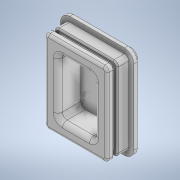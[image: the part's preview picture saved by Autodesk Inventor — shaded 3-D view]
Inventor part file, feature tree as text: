
AUTODESK INVENTOR PART (.ipt)
format: ipt  version: 2021 (Build 250183000, 183)  size: 454,144 bytes
history: native  units: mm
features: extrude x11, sketch x10, projected_geometry x5, chamfer x3, fillet x3
ambient origin geometry x8: Origin, YZ Plane, XZ Plane, XY Plane, X Axis, Y Axis, Z Axis, Center Point
bodies: Body1 (feature_tree)
feature tree (32):
  sketch  "Boceto1"  dims[d17=27.75mm d18=36.38mm]
  extrude  "Extrusión5"  Depth=36.38mm
  extrude  "Extrusión6"  Depth=2.0mm
  chamfer  "Chaflán2"  Distance=3.0mm
  extrude  "Extrusión7"  Depth=1.5mm TaperAngle=45.0deg
  extrude  "Extrusión8"  Depth=5.0mm
  extrude  "Extrusión9"  Depth=5.0mm
  chamfer  "Chaflán3"  Distance=5.0mm
  chamfer  "Chaflán4"  Distance=1.2mm
  extrude  "Extrusión11"  Depth=0.8mm TaperAngle=45.0deg
  fillet  "Empalme4"  Radius=10.0mm
  extrude  "Extrusión12"  Depth=2.0mm
  extrude  "Extrusión13"  Depth=10.0mm TaperAngle=0.0deg
  extrude  "Extrusión14"  Depth=2.0mm
  extrude  "Extrusión15"  Depth=2.0mm TaperAngle=0.0deg
  extrude  "Extrusión16"  Depth=2.0mm
  fillet  "Empalme7"  Radius=10.0mm
  fillet  "Empalme8"  Radius=10.0mm
  sketch  "Boceto4"  dims[d19=2.0mm d20=2.0mm d21=3.0mm d22=0.0mm]
  sketch  "Boceto5"  dims[d23=8.0mm d24=0.0mm d28=1.5mm d29=2.0mm d30=45.0deg]
  projected_geometry  "Contorno proyectado2"
  sketch  "Boceto6"  dims[d31=5.0mm d32=5.0mm]
  projected_geometry  "Contorno proyectado3"
  sketch  "Boceto8"  dims[d33=5.0mm d34=5.0mm d35=5.0mm d36=0.0mm]
  sketch  "Boceto9"  dims[d37=1.4mm]
  projected_geometry  "Contorno proyectado5"
  sketch  "Boceto10"  dims[d38=2.0mm d39=1.2mm d40=0.0mm]
  sketch  "Boceto11"  dims[d41=3.0mm d42=0.0mm d43=0.8mm d44=2.0mm d45=45.0deg]
  sketch  "Boceto12"  dims[d46=0.8mm d47=2.0mm d48=45.0deg d55=10.0mm d56=0.0mm]
  projected_geometry  "Contorno proyectado7"
  projected_geometry  "Contorno proyectado8"
  sketch  "Boceto13"  dims[d57=1.5mm d58=4.5mm d59=10.0mm d60=0.0mm d63=12.0mm d64=0.35mm d65=0.0mm d66=0.18mm d67=10.0mm d68=0.0mm d69=10.0mm d70=0.0mm d71=10.0mm d72=0.0mm d73=2.0mm d74=2.0mm]
